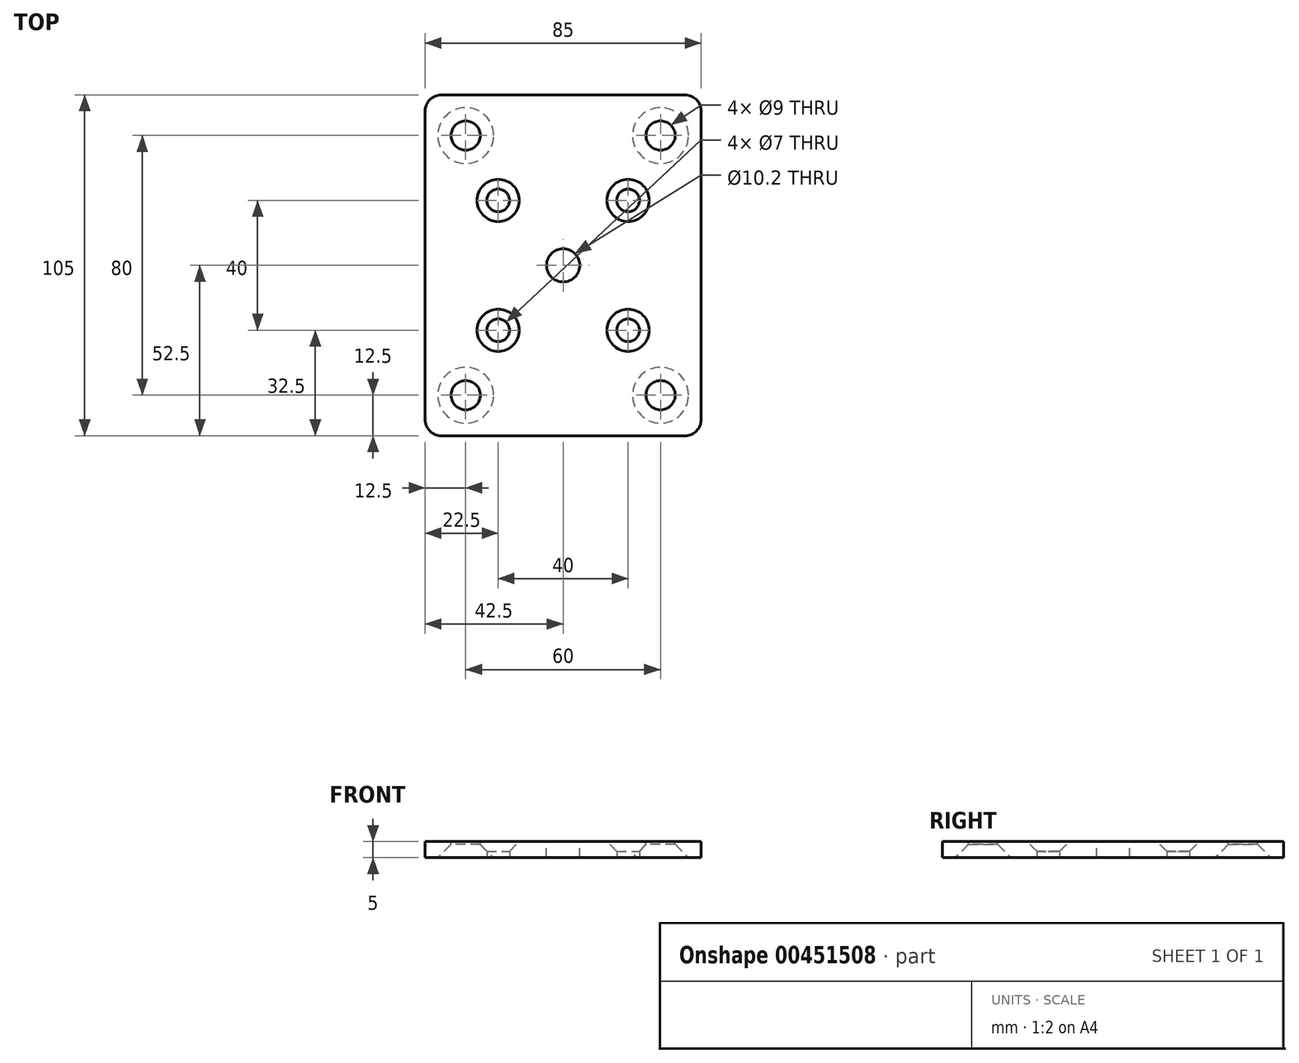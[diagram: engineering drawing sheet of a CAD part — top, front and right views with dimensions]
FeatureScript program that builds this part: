
annotation { "Feature Type Name" : "Feature", "Feature Type Description" : "" }
export const myFeature = defineFeature(function(context is Context, id is Id, definition is map)
    precondition{}
    {
        {
            var Q0;
            Q0=qCreatedBy(makeId("Top.planeOp"),FACE);
            var sketch = newSketch(context, id + "F0", { "sketchPlane" : qUnion([Q0])});
            skLineSegment(sketch, "E0.bottom", {"start": v(42.5, -52.5) * mm, "end": v(-42.5, -52.5) * mm});
            skLineSegment(sketch, "E0.top", {"start": v(42.5, 52.5) * mm, "end": v(-42.5, 52.5) * mm});
            skLineSegment(sketch, "E0.left", {"start": v(42.5, -52.5) * mm, "end": v(42.5, 52.5) * mm});
            skLineSegment(sketch, "E0.right", {"start": v(-42.5, -52.5) * mm, "end": v(-42.5, 52.5) * mm});
            skPoint(sketch, "E0.middle", {"position": v(0, 0) * mm});
            skSolve(sketch);
        }
        {
            var Q0;
            Q0=qSketchRegion(id+"F0",true);
            extrude(context, id + "F1", {"entities" : qUnion([Q0]), "oppositeDirection" : true, "depth" : 5 * mm});
        }
        {
            var Q0;
            Q0=makeQuery(id+"F1.opExtrude","CAP_FACE",FACE,{"disambiguationData":[OSD([sQuery(id+"F0.wireOp",EDGE,"E0.bottom"),sQuery(id+"F0.wireOp",EDGE,"E0.top"),sQuery(id+"F0.wireOp",EDGE,"E0.left"),sQuery(id+"F0.wireOp",EDGE,"E0.right")])],"isStart":true});
            var sketch = newSketch(context, id + "F2", { "sketchPlane" : qUnion([Q0])});
            skCircle(sketch, "E1", {"center": v(0, 0) * mm, "radius": 5.1 * mm});
            skCircle(sketch, "E2", {"center": v(30, 40) * mm, "radius": 4.5 * mm});
            skCircle(sketch, "E3", {"center": v(-30, 40) * mm, "radius": 4.5 * mm});
            skCircle(sketch, "E4", {"center": v(-30, -40) * mm, "radius": 4.5 * mm});
            skCircle(sketch, "E5", {"center": v(30, -40) * mm, "radius": 4.5 * mm});
            skSolve(sketch);
        }
        {
            var Q0;
            Q0=qSketchRegion(id+"F2",true);
            extrude(context, id + "F3", {"entities" : qUnion([Q0]), "operationType" : NewBodyOperationType.REMOVE, "endBound" : BoundingType.THROUGH_ALL, "oppositeDirection" : true, "depth" : 25 * mm});
        }
        {
            var Q0;
            Q0=makeQuery(id+"F1.opExtrude","CAP_FACE",FACE,{"disambiguationData":[OSD([sQuery(id+"F0.wireOp",EDGE,"E0.bottom"),sQuery(id+"F0.wireOp",EDGE,"E0.top"),sQuery(id+"F0.wireOp",EDGE,"E0.left"),sQuery(id+"F0.wireOp",EDGE,"E0.right")])],"isStart":true});
            var sketch = newSketch(context, id + "F4", { "sketchPlane" : qUnion([Q0])});
            skPoint(sketch, "E6", {"position": v(-20, 20) * mm});
            skPoint(sketch, "E7", {"position": v(20, 20) * mm});
            skPoint(sketch, "E8", {"position": v(20, -20) * mm});
            skPoint(sketch, "E9", {"position": v(-20, -20) * mm});
            skSolve(sketch);
        }
        {
            var Q0;
            Q0=sQuery(id+"F4.wireOp",VERTEX,"E6");
            var Q1;
            Q1=sQuery(id+"F4.wireOp",VERTEX,"E7");
            var Q2;
            Q2=sQuery(id+"F4.wireOp",VERTEX,"E8");
            var Q3;
            Q3=sQuery(id+"F4.wireOp",VERTEX,"E9");
            var Q4;
            Q4=makeQuery(id+"F1.opExtrude","SWEPT_BODY",BODY,{"disambiguationData":[OSD([sQuery(id+"F0.wireOp",EDGE,"E0.bottom"),sQuery(id+"F0.wireOp",EDGE,"E0.top"),sQuery(id+"F0.wireOp",EDGE,"E0.left"),sQuery(id+"F0.wireOp",EDGE,"E0.right")])]});
            hole(context, id + "F5", {"style" : HoleStyle.C_SINK, "endStyle" : HoleEndStyle.THROUGH, "holeDiameter" : 7 * mm, "cSinkDiameter" : 13 * mm, "cSinkAngle" : 90 * degree, "locations" : qUnion([Q0, Q1, Q2, Q3]), "scope" : qUnion([Q4]), "isTappedThrough" : true, "startStyle" : HoleStartStyle.PART});
        }
        {
            var Q0;
            Q0=makeQuery(id+"F1.opExtrude","SWEPT_EDGE",EDGE,{"disambiguationData":[OSD([sQuery(id+"F0.wireOp",EDGE,"E0.bottom"),sQuery(id+"F0.wireOp",EDGE,"E0.right")])]});
            var Q1;
            Q1=makeQuery(id+"F1.opExtrude","SWEPT_EDGE",EDGE,{"disambiguationData":[OSD([sQuery(id+"F0.wireOp",EDGE,"E0.bottom"),sQuery(id+"F0.wireOp",EDGE,"E0.left")])]});
            var Q2;
            Q2=makeQuery(id+"F1.opExtrude","SWEPT_EDGE",EDGE,{"disambiguationData":[OSD([sQuery(id+"F0.wireOp",EDGE,"E0.top"),sQuery(id+"F0.wireOp",EDGE,"E0.left")])]});
            var Q3;
            Q3=makeQuery(id+"F1.opExtrude","SWEPT_EDGE",EDGE,{"disambiguationData":[OSD([sQuery(id+"F0.wireOp",EDGE,"E0.top"),sQuery(id+"F0.wireOp",EDGE,"E0.right")])]});
            fillet(context, id + "F6", {"entities" : qUnion([Q0, Q1, Q2, Q3]), "radius" : 5 * mm, "tangentPropagation" : true, "allowEdgeOverflow" : false});
        }
        {
            var Q0;
            Q0=makeQuery(id+"F3.boolean.opBoolean","INTERSECT",EDGE,{"derivedFrom":[makeQuery(id+"F1.opExtrude","CAP_FACE",FACE,{"disambiguationData":[OSD([sQuery(id+"F0.wireOp",EDGE,"E0.bottom"),sQuery(id+"F0.wireOp",EDGE,"E0.top"),sQuery(id+"F0.wireOp",EDGE,"E0.left"),sQuery(id+"F0.wireOp",EDGE,"E0.right")])],"isStart":false}),makeQuery(id+"F3.opExtrude","SWEPT_FACE",FACE,{"disambiguationData":[OSD([sQuery(id+"F2.wireOp",EDGE,"E2")])]})]});
            var Q1;
            Q1=makeQuery(id+"F3.boolean.opBoolean","INTERSECT",EDGE,{"derivedFrom":[makeQuery(id+"F1.opExtrude","CAP_FACE",FACE,{"disambiguationData":[OSD([sQuery(id+"F0.wireOp",EDGE,"E0.bottom"),sQuery(id+"F0.wireOp",EDGE,"E0.top"),sQuery(id+"F0.wireOp",EDGE,"E0.left"),sQuery(id+"F0.wireOp",EDGE,"E0.right")])],"isStart":false}),makeQuery(id+"F3.opExtrude","SWEPT_FACE",FACE,{"disambiguationData":[OSD([sQuery(id+"F2.wireOp",EDGE,"E3")])]})]});
            var Q2;
            Q2=makeQuery(id+"F3.boolean.opBoolean","INTERSECT",EDGE,{"derivedFrom":[makeQuery(id+"F1.opExtrude","CAP_FACE",FACE,{"disambiguationData":[OSD([sQuery(id+"F0.wireOp",EDGE,"E0.bottom"),sQuery(id+"F0.wireOp",EDGE,"E0.top"),sQuery(id+"F0.wireOp",EDGE,"E0.left"),sQuery(id+"F0.wireOp",EDGE,"E0.right")])],"isStart":false}),makeQuery(id+"F3.opExtrude","SWEPT_FACE",FACE,{"disambiguationData":[OSD([sQuery(id+"F2.wireOp",EDGE,"E4")])]})]});
            var Q3;
            Q3=makeQuery(id+"F3.boolean.opBoolean","INTERSECT",EDGE,{"derivedFrom":[makeQuery(id+"F1.opExtrude","CAP_FACE",FACE,{"disambiguationData":[OSD([sQuery(id+"F0.wireOp",EDGE,"E0.bottom"),sQuery(id+"F0.wireOp",EDGE,"E0.top"),sQuery(id+"F0.wireOp",EDGE,"E0.left"),sQuery(id+"F0.wireOp",EDGE,"E0.right")])],"isStart":false}),makeQuery(id+"F3.opExtrude","SWEPT_FACE",FACE,{"disambiguationData":[OSD([sQuery(id+"F2.wireOp",EDGE,"E5")])]})]});
            chamfer(context, id + "F7", {"entities" : qUnion([Q0, Q1, Q2, Q3]), "width" : 4.1 * mm, "tangentPropagation" : true});
        }
    });
